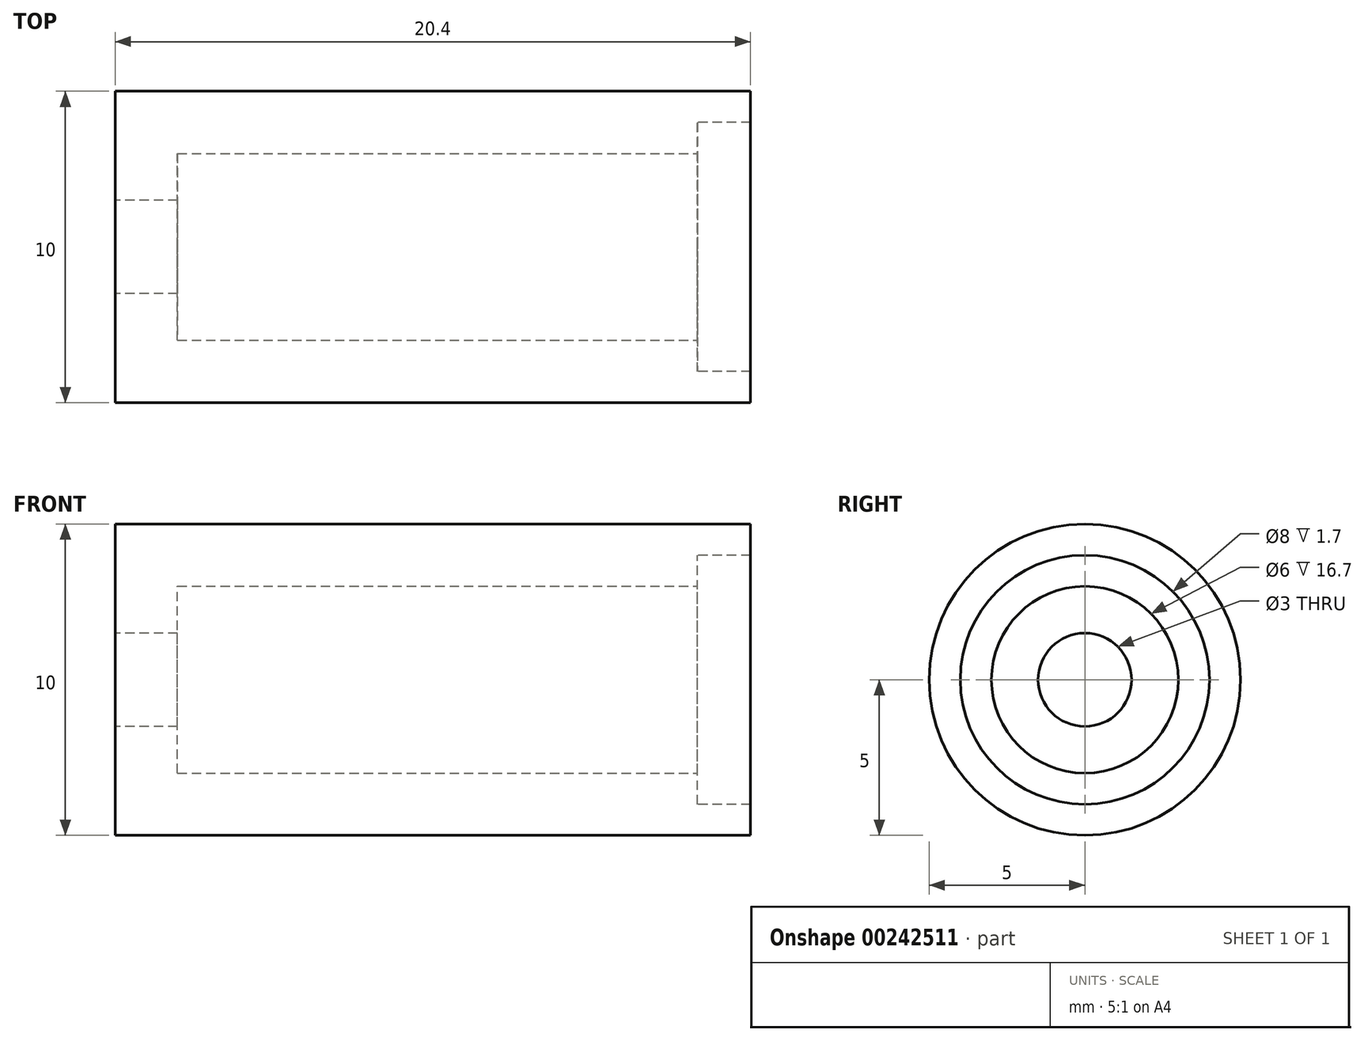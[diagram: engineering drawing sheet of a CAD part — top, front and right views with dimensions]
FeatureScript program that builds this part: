
annotation { "Feature Type Name" : "Feature", "Feature Type Description" : "" }
export const myFeature = defineFeature(function(context is Context, id is Id, definition is map)
    precondition{}
    {
        {
            var Q0;
            Q0=qCreatedBy(makeId("Right.planeOp"),FACE);
            var sketch = newSketch(context, id + "F0", { "sketchPlane" : qUnion([Q0])});
            skCircle(sketch, "E0", {"center": v(0, 0) * mm, "radius": 5 * mm});
            skCircle(sketch, "E1", {"center": v(0, 0) * mm, "radius": 4 * mm});
            skSolve(sketch);
        }
        {
            var Q0;
            Q0=makeQuery(id+"F0.imprint","IMPRINT",FACE,{"disambiguationData":[TD([[makeQuery(id+"F0.imprint","IMPRINT",EDGE,{"derivedFrom":sQuery(id+"F0.wireOp",EDGE,"E0")}),1.0]])]});
            var Q1;
            Q1=makeQuery(id+"F0.imprint","IMPRINT",FACE,{"disambiguationData":[TD([[makeQuery(id+"F0.imprint","IMPRINT",EDGE,{"derivedFrom":sQuery(id+"F0.wireOp",EDGE,"E1")}),1.0]])]});
            extrude(context, id + "F1", {"entities" : qUnion([Q0, Q1]), "depth" : 2 * mm, "hasSecondDirection" : true, "secondDirectionOppositeDirection" : true, "secondDirectionDepth" : 0 * mm});
        }
        {
            var Q0;
            Q0 = qSketchRegion(id + "F0", true);
            extrude(context, id + "F2", {"entities" : qUnion([Q0]), "operationType" : NewBodyOperationType.ADD, "depth" : 20.4 * mm, "hasSecondDirection" : true, "secondDirectionOppositeDirection" : false, "secondDirectionDepth" : 0 * mm});
        }
        {
            var Q0;
            Q0=qCreatedBy(makeId("Right.planeOp"),FACE);
            cPlane(context, id + "F3", {"entities" : qUnion([Q0]), "cplaneType" : CPlaneType.OFFSET, "offset" : 21.9 * mm, "width" : 150 * mm, "height" : 150 * mm});
        }
        {
            var Q0;
            Q0=qCreatedBy(id+"F3.planeOp",FACE);
            var sketch = newSketch(context, id + "F4", { "sketchPlane" : qUnion([Q0])});
            skCircle(sketch, "E2.0", {"center": v(0, 0) * mm, "radius": 4 * mm});
            skCircle(sketch, "E3", {"center": v(0, 0) * mm, "radius": 3 * mm});
            skSolve(sketch);
        }
        {
            var Q0;
            Q0 = qSketchRegion(id + "F4", true);
            extrude(context, id + "F5", {"entities" : qUnion([Q0]), "operationType" : NewBodyOperationType.ADD, "oppositeDirection" : true, "depth" : 21 * mm, "hasSecondDirection" : true, "secondDirectionOppositeDirection" : true, "secondDirectionDepth" : 3.2 * mm});
        }
        {
            var Q0;
            Q0=qCreatedBy(makeId("Right.planeOp"),FACE);
            var sketch = newSketch(context, id + "F6", { "sketchPlane" : qUnion([Q0])});
            skCircle(sketch, "E4", {"center": v(0, 0) * mm, "radius": 1.5 * mm});
            skSolve(sketch);
        }
        {
            var Q0;
            Q0=makeQuery(id+"F6.imprint","IMPRINT",FACE,{"disambiguationData":[TD([[makeQuery(id+"F6.imprint","IMPRINT",EDGE,{"derivedFrom":sQuery(id+"F6.wireOp",EDGE,"E4")}),1.0]])]});
            var Q1;
            Q1=sQuery(id+"F6.wireOp",EDGE,"E4");
            extrude(context, id + "F7", {"entities" : qUnion([Q0]), "operationType" : NewBodyOperationType.REMOVE, "surfaceEntities" : qUnion([Q1]), "depth" : 5.6 * mm});
        }
    });
